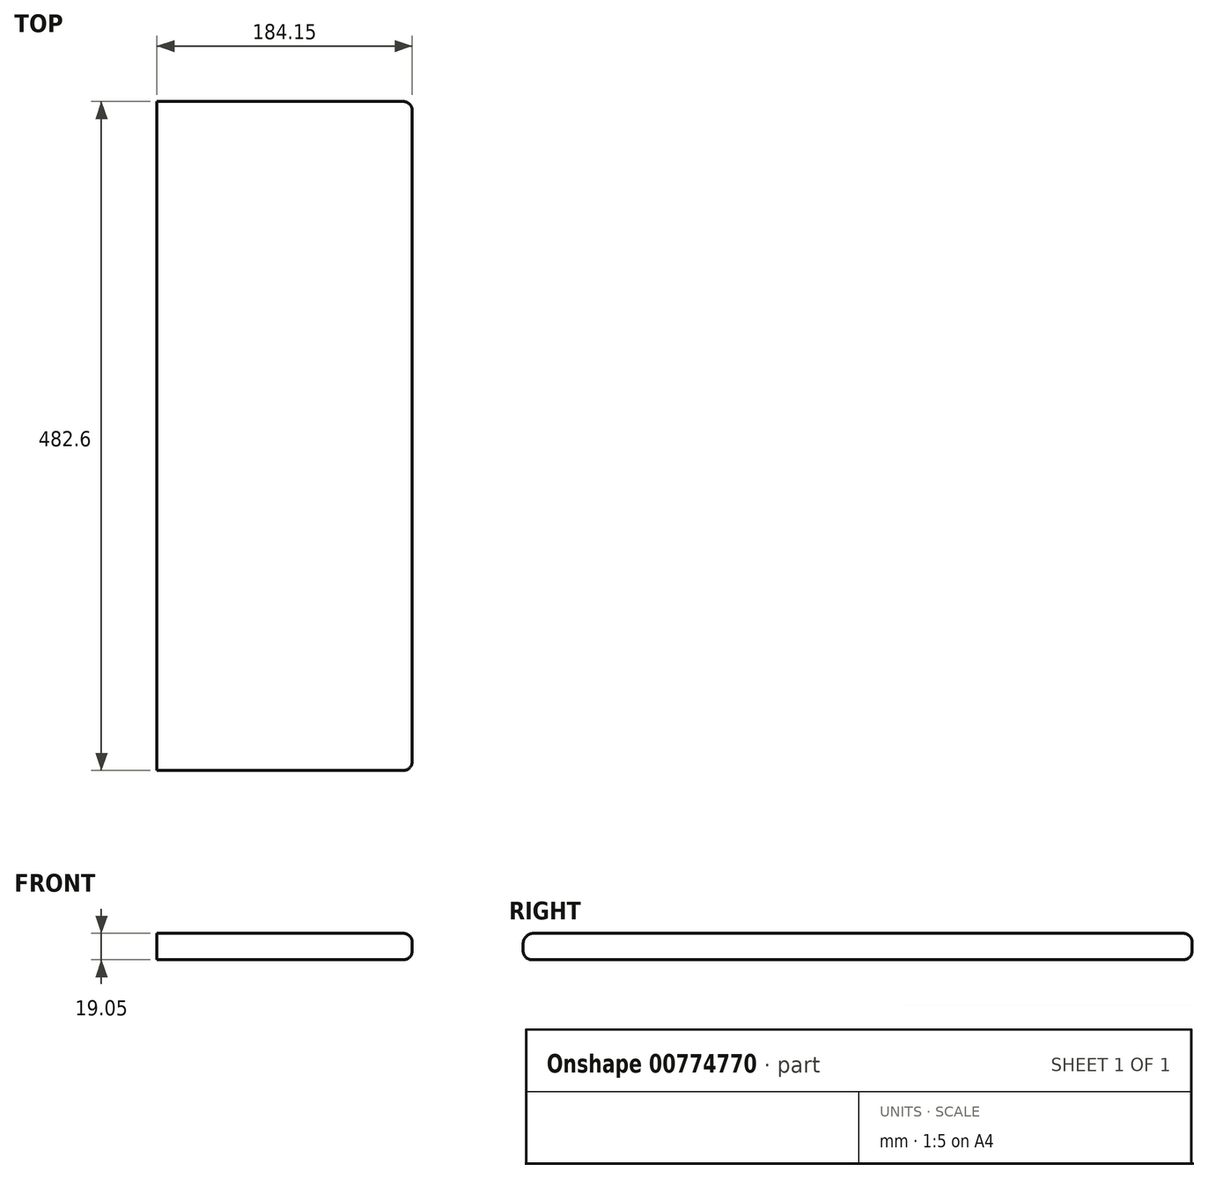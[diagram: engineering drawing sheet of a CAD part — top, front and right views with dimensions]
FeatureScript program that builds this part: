
annotation { "Feature Type Name" : "Feature", "Feature Type Description" : "" }
export const myFeature = defineFeature(function(context is Context, id is Id, definition is map)
    precondition{}
    {
        {
            var Q0;
            Q0=qCreatedBy(makeId("Front.planeOp"),FACE);
            var sketch = newSketch(context, id + "F0", { "sketchPlane" : qUnion([Q0])});
            skLineSegment(sketch, "E0.bottom", {"start": v(0, 0) * mm, "end": v(184.15, 0) * mm});
            skLineSegment(sketch, "E0.top", {"start": v(0, -19.05) * mm, "end": v(184.15, -19.05) * mm});
            skLineSegment(sketch, "E0.left", {"start": v(0, 0) * mm, "end": v(0, -19.05) * mm});
            skLineSegment(sketch, "E0.right", {"start": v(184.15, 0) * mm, "end": v(184.15, -19.05) * mm});
            skSolve(sketch);
        }
        {
            var Q0;
            Q0 = qSketchRegion(id + "F0", true);
            extrude(context, id + "F1", {"entities" : qUnion([Q0]), "depth" : 482.6 * mm, "offsetDistance" : 25.4 * mm});
        }
        {
            var Q0;
            Q0=makeQuery(id+"F1.opExtrude","CAP_EDGE",EDGE,{"disambiguationData":[OSD([sQuery(id+"F0.wireOp",EDGE,"E0.bottom")])],"isStart":false});
            fillet(context, id + "F2", {"entities" : qUnion([Q0]), "radius" : 7.62 * mm, "tangentPropagation" : true, "allowEdgeOverflow" : false});
        }
        {
            var Q0;
            Q0=makeQuery(id+"F1.opExtrude","CAP_EDGE",EDGE,{"disambiguationData":[OSD([sQuery(id+"F0.wireOp",EDGE,"E0.top")])],"isStart":false});
            fillet(context, id + "F3", {"entities" : qUnion([Q0]), "radius" : 6.35 * mm, "tangentPropagation" : true, "allowEdgeOverflow" : false});
        }
        {
            var Q0;
            Q0=makeQuery(id+"F1.opExtrude","SWEPT_EDGE",EDGE,{"disambiguationData":[OSD([sQuery(id+"F0.wireOp",EDGE,"E0.top"),sQuery(id+"F0.wireOp",EDGE,"E0.right")])]});
            fillet(context, id + "F4", {"entities" : qUnion([Q0]), "radius" : 6.35 * mm, "tangentPropagation" : true, "allowEdgeOverflow" : false});
        }
        {
            var Q0;
            Q0=makeQuery(id+"F1.opExtrude","CAP_EDGE",EDGE,{"disambiguationData":[OSD([sQuery(id+"F0.wireOp",EDGE,"E0.top")])],"isStart":true});
            fillet(context, id + "F5", {"entities" : qUnion([Q0]), "radius" : 6.35 * mm, "tangentPropagation" : true, "allowEdgeOverflow" : false});
        }
    });
